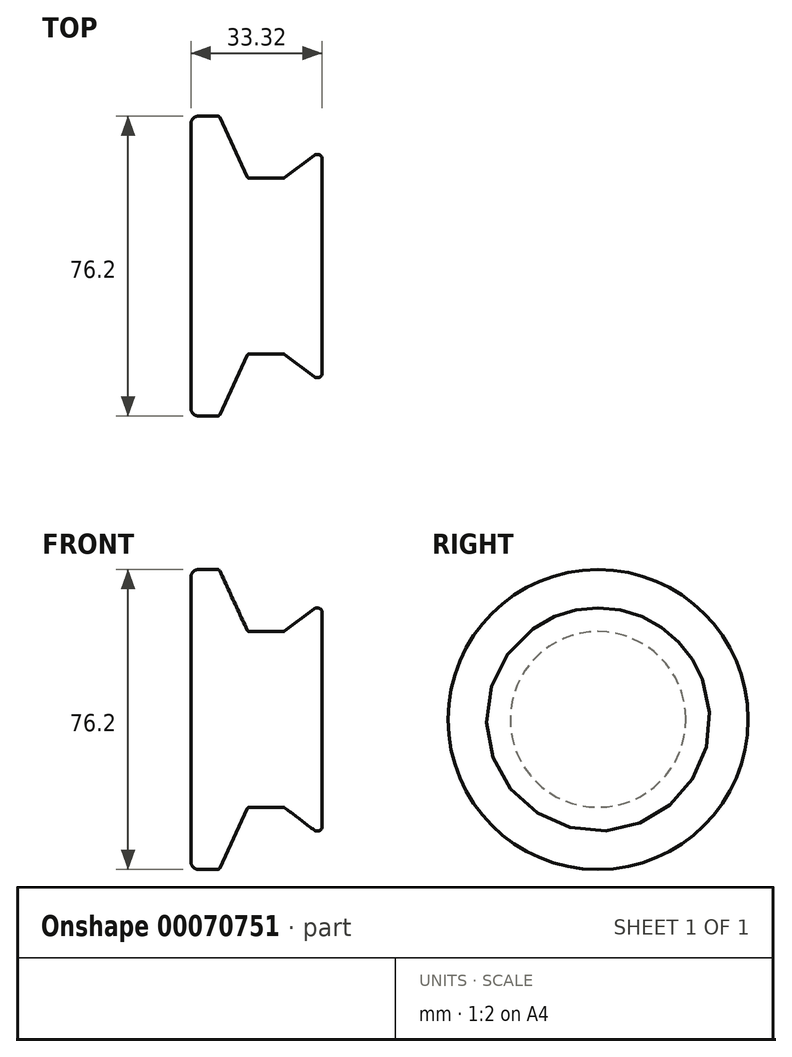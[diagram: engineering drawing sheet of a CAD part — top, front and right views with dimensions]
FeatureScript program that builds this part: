
annotation { "Feature Type Name" : "Feature", "Feature Type Description" : "" }
export const myFeature = defineFeature(function(context is Context, id is Id, definition is map)
    precondition{}
    {
        {
            var Q0;
            Q0=qCreatedBy(makeId("Front.planeOp"),FACE);
            var sketch = newSketch(context, id + "F0", { "sketchPlane" : qUnion([Q0])});
            skLineSegment(sketch, "E0", {"start": v(0, 0) * mm, "end": v(33.32, 0) * mm});
            skLineSegment(sketch, "E1", {"start": v(33.32, 0) * mm, "end": v(33.32, 29.66) * mm});
            skLineSegment(sketch, "E2", {"start": v(7.17, 38.1) * mm, "end": v(0, 38.1) * mm});
            skLineSegment(sketch, "E3", {"start": v(0, 38.1) * mm, "end": v(0, 0) * mm});
            skLineSegment(sketch, "E4", {"start": v(7.17, 38.1) * mm, "end": v(14.47, 22.31) * mm});
            skLineSegment(sketch, "E5", {"start": v(14.47, 22.31) * mm, "end": v(23.66, 22.31) * mm});
            skLineSegment(sketch, "E6", {"start": v(23.66, 22.31) * mm, "end": v(33.32, 29.66) * mm});
            skSolve(sketch);
        }
        {
            var Q0;
            Q0 = qSketchRegion(id + "F0", true);
            var Q1;
            Q1=sQuery(id+"F0.wireOp",EDGE,"E0");
            revolve(context, id + "F1", {"entities" : qUnion([Q0]), "axis" : qUnion([Q1]), "revolveType" : RevolveType.FULL});
        }
        {
            var Q0;
            Q0=makeQuery(id+"F1.opRevolve","SWEPT_EDGE",EDGE,{"disambiguationData":[OSD([sQuery(id+"F0.wireOp",EDGE,"E2"),sQuery(id+"F0.wireOp",EDGE,"E3")])]});
            fillet(context, id + "F2", {"entities" : qUnion([Q0]), "radius" : 1.9 * mm, "tangentPropagation" : true, "allowEdgeOverflow" : false});
        }
        {
            var Q0;
            Q0=makeQuery(id+"F1.opRevolve","SWEPT_EDGE",EDGE,{"disambiguationData":[OSD([sQuery(id+"F0.wireOp",EDGE,"E2"),sQuery(id+"F0.wireOp",EDGE,"E4")])]});
            var Q1;
            Q1=makeQuery(id+"F1.opRevolve","SWEPT_EDGE",EDGE,{"disambiguationData":[OSD([sQuery(id+"F0.wireOp",EDGE,"E4"),sQuery(id+"F0.wireOp",EDGE,"E5")])]});
            var Q2;
            Q2=makeQuery(id+"F1.opRevolve","SWEPT_EDGE",EDGE,{"disambiguationData":[OSD([sQuery(id+"F0.wireOp",EDGE,"E5"),sQuery(id+"F0.wireOp",EDGE,"E6")])]});
            fillet(context, id + "F3", {"entities" : qUnion([Q0, Q1, Q2]), "radius" : 0.64 * mm, "tangentPropagation" : true, "allowEdgeOverflow" : false});
        }
        {
            var Q0;
            Q0=makeQuery(id+"F1.opRevolve","SWEPT_EDGE",EDGE,{"disambiguationData":[OSD([sQuery(id+"F0.wireOp",EDGE,"E1"),sQuery(id+"F0.wireOp",EDGE,"E6")])]});
            fillet(context, id + "F4", {"entities" : qUnion([Q0]), "radius" : 1.27 * mm, "tangentPropagation" : true, "allowEdgeOverflow" : false});
        }
    });
